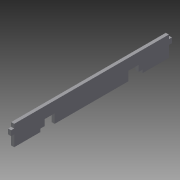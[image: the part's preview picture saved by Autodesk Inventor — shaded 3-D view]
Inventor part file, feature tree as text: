
AUTODESK INVENTOR PART (.ipt)
format: ipt  version: 2015 (Build 190159000, 159)  size: 107,008 bytes
history: native  units: mm
features: extrude x1, sketch x1
ambient origin geometry x8: Origin, YZ Plane, XZ Plane, XY Plane, X Axis, Y Axis, Z Axis, Center Point
bodies: Body1 (feature_tree)
feature tree (2):
  extrude  "Extrusion2"  Depth=153.0mm
  sketch  "Sketch1"  dims[d0=20.0mm d1=153.0mm d2=5.0mm d3=3.0mm d4=11.0mm d5=3.0mm d6=5.0mm d7=10.0mm d9=30.0mm d11=10.0mm d12=30.0mm d21=11.0mm d25=4.0mm d26=3.0mm d28=4.0mm d30=9.0mm d31=9.0mm d32=9.0mm d33=20.0mm d34=3.0mm d35=26.0mm d36=3.0mm d37=0.0mm]
